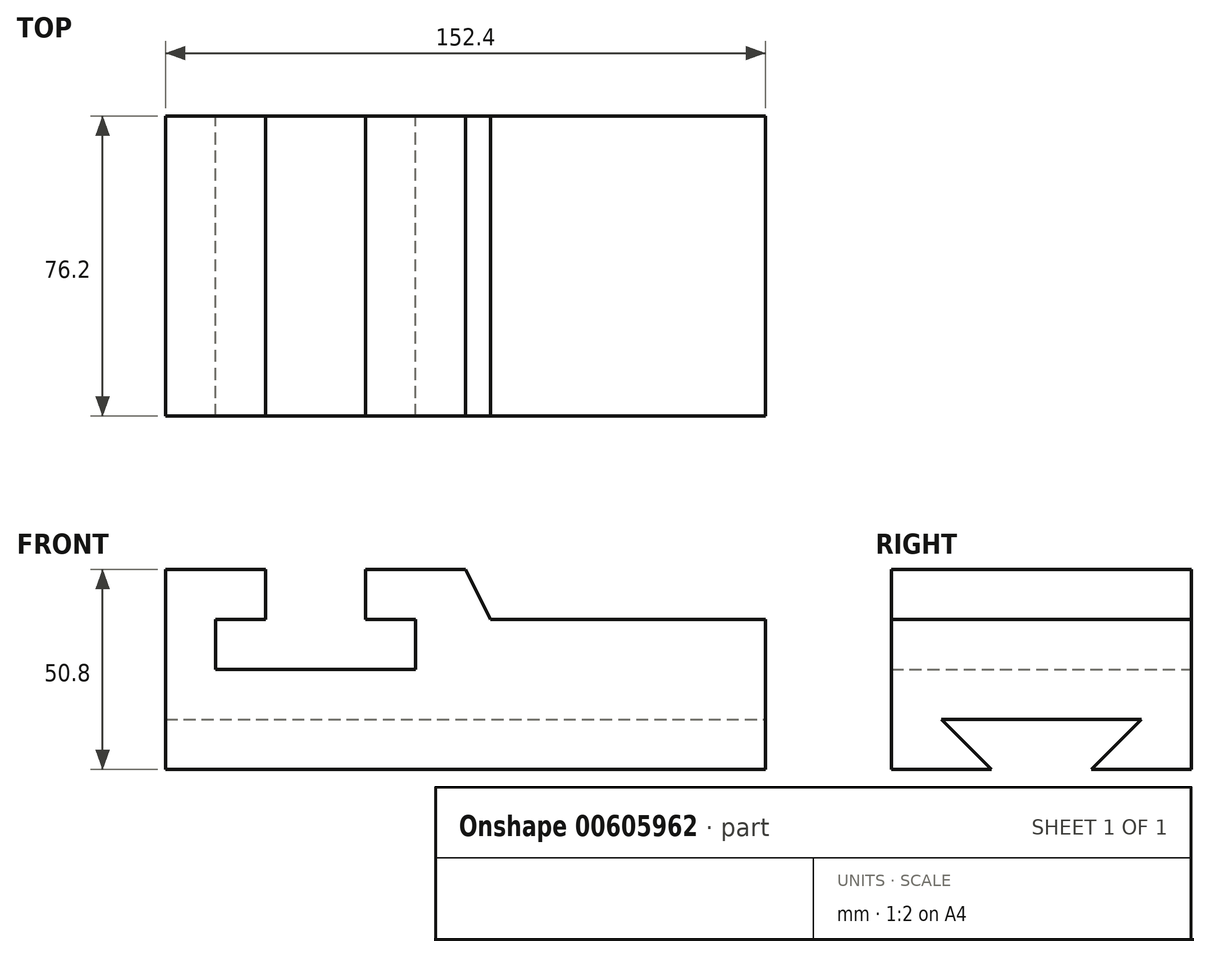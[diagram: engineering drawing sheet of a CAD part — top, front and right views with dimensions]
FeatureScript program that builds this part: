
annotation { "Feature Type Name" : "Feature", "Feature Type Description" : "" }
export const myFeature = defineFeature(function(context is Context, id is Id, definition is map)
    precondition{}
    {
        {
            var Q0;
            Q0=qCreatedBy(makeId("Front.planeOp"),FACE);
            var sketch = newSketch(context, id + "F0", { "sketchPlane" : qUnion([Q0])});
            skLineSegment(sketch, "E0", {"start": v(-223.14, -25.4) * mm, "end": v(-70.74, -25.4) * mm});
            skLineSegment(sketch, "E1", {"start": v(-223.14, -25.4) * mm, "end": v(-223.14, 25.4) * mm});
            skLineSegment(sketch, "E2", {"start": v(-223.14, 25.4) * mm, "end": v(-197.74, 25.4) * mm});
            skLineSegment(sketch, "E3", {"start": v(-197.74, 25.4) * mm, "end": v(-197.74, 12.7) * mm});
            skLineSegment(sketch, "E4", {"start": v(-197.74, 12.7) * mm, "end": v(-210.44, 12.7) * mm});
            skLineSegment(sketch, "E5", {"start": v(-210.44, 12.7) * mm, "end": v(-210.44, 0) * mm});
            skLineSegment(sketch, "E6", {"start": v(-210.44, 0) * mm, "end": v(-159.64, 0) * mm});
            skLineSegment(sketch, "E7", {"start": v(-159.64, 0) * mm, "end": v(-159.64, 12.7) * mm});
            skLineSegment(sketch, "E8", {"start": v(-159.64, 12.7) * mm, "end": v(-172.34, 12.7) * mm});
            skLineSegment(sketch, "E9", {"start": v(-172.34, 12.7) * mm, "end": v(-172.34, 25.4) * mm});
            skLineSegment(sketch, "E10", {"start": v(-172.34, 25.4) * mm, "end": v(-146.94, 25.4) * mm});
            skLineSegment(sketch, "E11", {"start": v(-70.74, -25.4) * mm, "end": v(-70.74, 12.7) * mm});
            skLineSegment(sketch, "E12", {"start": v(-140.59, 12.7) * mm, "end": v(-70.74, 12.7) * mm});
            skLineSegment(sketch, "E13", {"start": v(-146.94, 25.4) * mm, "end": v(-140.59, 12.7) * mm});
            skSolve(sketch);
        }
        {
            var Q0;
            Q0 = qSketchRegion(id + "F0", true);
            extrude(context, id + "F1", {"entities" : qUnion([Q0]), "depth" : 76.2 * mm, "offsetDistance" : 25.4 * mm});
        }
        {
            var Q0;
            Q0=makeQuery(id+"F1.opExtrude","SWEPT_FACE",FACE,{"disambiguationData":[OSD([sQuery(id+"F0.wireOp",EDGE,"E11")])]});
            var sketch = newSketch(context, id + "F2", { "sketchPlane" : qUnion([Q0])});
            skLineSegment(sketch, "E14", {"start": v(-38.1, -12.7) * mm, "end": v(-63.5, -12.7) * mm});
            skLineSegment(sketch, "E15", {"start": v(-38.1, -12.7) * mm, "end": v(-12.7, -12.7) * mm});
            skLineSegment(sketch, "E16", {"start": v(-12.7, -12.7) * mm, "end": v(-25.4, -25.4) * mm});
            skLineSegment(sketch, "E17", {"start": v(-63.5, -12.7) * mm, "end": v(-50.8, -25.4) * mm});
            skLineSegment(sketch, "E18", {"start": v(-50.8, -25.4) * mm, "end": v(-25.4, -25.4) * mm});
            skSolve(sketch);
        }
        {
            var Q0;
            Q0=makeQuery(id+"F2.imprint","IMPRINT",FACE,{"disambiguationData":[TD([[makeQuery(id+"F2.imprint","IMPRINT",EDGE,{"derivedFrom":sQuery(id+"F2.wireOp",EDGE,"E14")}),1.0]])]});
            extrude(context, id + "F3", {"entities" : qUnion([Q0]), "operationType" : NewBodyOperationType.REMOVE, "oppositeDirection" : true, "depth" : 166.37 * mm, "offsetDistance" : 25.4 * mm});
        }
    });
